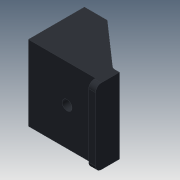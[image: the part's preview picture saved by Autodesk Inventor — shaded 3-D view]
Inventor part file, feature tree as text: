
AUTODESK INVENTOR PART (.ipt)
format: ipt  version: 2020.3 (Build 243373000, 373)  size: 193,536 bytes
history: native  units: in
note: dims shown in document units (in); Inventor stores cm internally (conversion verified against a paired STEP export)
features: sketch x8, extrude x6, hole x2, projected_geometry x2, fillet x1
ambient origin geometry x8: Origin, YZ Plane, XZ Plane, XY Plane, X Axis, Y Axis, Z Axis, Center Point
bodies: Body1 (feature_tree)
feature tree (19):
  extrude  "Extrusion3"  Depth=1.65in TaperAngle=0.0deg
  hole  "Hole1"  [1 undecoded]
  extrude  "Extrusion4"  Depth=0.5in
  hole  "Hole2"  [1 undecoded]
  extrude  "Extrusion5"  Depth=0.25in
  extrude  "Extrusion6"  Depth=0.195in
  extrude  "Extrusion7"  Depth=0.45in
  extrude  "Extrusion8"  Depth=0.35in TaperAngle=0.0deg
  fillet  "Fillet2"  [1 undecoded]
  sketch  "Sketch1"  dims[d10=0.375in d15=1.65in d16=0.0in]
  sketch  "Sketch2"  dims[d20=0.217in d21=0.75in d22=0.375in d23=0.25in d24=0.5635in d25=1.0in d26=0.8108in d27=0.25in d28=0.0in]
  projected_geometry  "Projected Loop1"
  sketch  "Sketch3"  dims[d36=1.23in d37=0.5in]
  sketch  "Sketch4"  dims[d38=1.475in d39=0.45in]
  sketch  "Sketch5"  dims[d40=0.45in d41=0.25in]
  sketch  "Sketch6"  dims[d42=0.096in d43=0.75in d44=0.172in d45=0.25in d46=0.6871in d47=0.4in d48=0.8108in d49=0.195in]
  sketch  "Sketch7"  dims[d50=0.07in d51=0.45in]
  sketch  "Sketch8"  dims[d52=0.4in d53=0.0in d54=0.35in d55=0.0in d56=0.0in d57=0.85in d58=0.3in d59=0.45in d60=0.25in d61=0.0in d63=0.5in d64=0.46in d65=15.0deg d66=0.25in d67=0.0in d68=0.0in d69=0.15in d70=0.15in d71=0.0in d72=0.125in]
  projected_geometry  "Projected Loop2"
note: 3 required parameter values undecoded (feature->parameter linkage not recoverable at this tier; creation-order binding heuristic only, values carry confidence <= 0.55)
